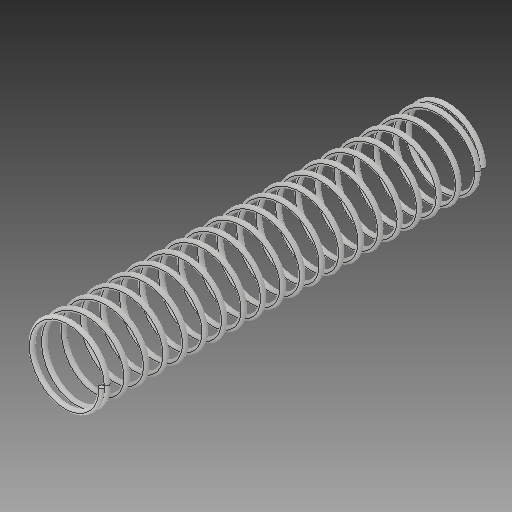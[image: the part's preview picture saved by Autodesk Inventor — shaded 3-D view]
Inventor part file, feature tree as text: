
AUTODESK INVENTOR PART (.ipt)
format: ipt  version: 2018 (Build 220112000, 112)  size: 913,408 bytes
history: native  units: in
note: dims shown in document units (in); Inventor stores cm internally (conversion verified against a paired STEP export)
features: sweep x1
ambient origin geometry x8: Origin, YZ Plane, XZ Plane, XY Plane, X Axis, Y Axis, Z Axis, Center Point
bodies: Solid1 (feature_tree)
feature tree (1):
  sweep  "Sweep1"
